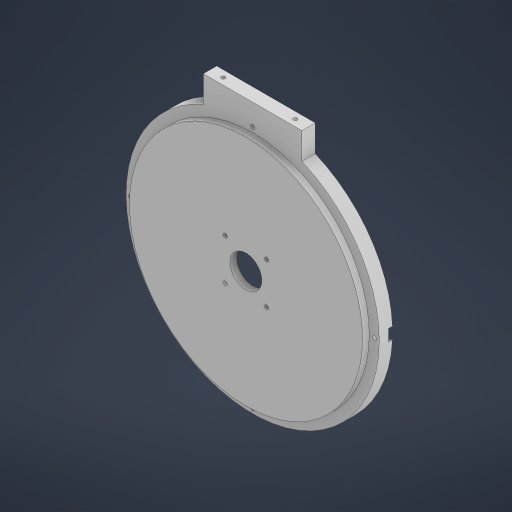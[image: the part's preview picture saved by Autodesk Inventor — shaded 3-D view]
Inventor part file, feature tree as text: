
AUTODESK INVENTOR PART (.ipt)
format: ipt  version: 2023 (Build 270158000, 158)  size: 283,136 bytes
history: native  units: mm
features: extrude x9, sketch x7
ambient origin geometry x8: Origin, YZ Plane, XZ Plane, XY Plane, X Axis, Y Axis, Z Axis, Center Point
bodies: Solid1 (feature_tree)
feature tree (16):
  extrude  "Extrusion1"  Depth=10.0mm TaperAngle=0.0deg
  sketch  "Sketch2"  dims[d4=175.0mm d5=10.0mm d6=0.0mm]
  extrude  "Extrusion2"  Depth=10.0mm TaperAngle=0.0deg
  extrude  "Extrusion3"  Depth=5.0mm
  sketch  "Sketch3"  dims[d7=5.0mm d8=0.0mm d13=47.0mm]
  extrude  "Extrusion8"  Depth=23.5mm
  sketch  "Sketch8"  dims[d27=3.0mm d28=3.0mm]
  extrude  "Extrusion10"  Depth=3.0mm
  extrude  "Extrusion11"  Depth=3.0mm
  extrude  "Extrusion7"  Depth=10.0mm TaperAngle=0.0deg
  extrude  "Extrusion9"  Depth=3.0mm
  extrude  "Extrusion12"  Depth=10.0mm
  sketch  "Sketch1"  dims[d0=190.0mm d2=10.0mm d3=0.0mm]
  sketch  "Sketch6"  dims[d14=47.0mm d15=23.5mm]
  sketch  "Sketch7"  dims[d16=23.5mm d26=3.0mm]
  sketch  "Sketch9"  dims[d29=3.0mm d30=70.0mm d31=0.0mm d34=3.0mm d35=24.0mm d36=10.0mm d37=0.0mm d38=11.0mm d39=11.0mm d40=11.0mm d41=11.0mm d42=3.0mm d43=0.0mm d44=180.0deg d45=20.0mm d46=10.0mm d47=0.0mm d48=10.0mm d49=0.0mm d50=10.0mm d51=10.0mm d52=3.0mm d53=3.0mm d54=10.0mm d55=0.0mm]
